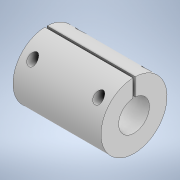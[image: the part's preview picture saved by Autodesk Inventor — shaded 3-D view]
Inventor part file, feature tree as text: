
AUTODESK INVENTOR PART (.ipt)
format: ipt  version: 2021.3 (Build 253353000, 353)  size: 143,360 bytes
history: native  units: mm
features: extrude x3, sketch x3, plane x2
ambient origin geometry x8: Origin, YZ Plane, XZ Plane, XY Plane, X Axis, Y Axis, Z Axis, Center Point
bodies: Solid1 (feature_tree)
feature tree (8):
  extrude  "Extrusion1"  Depth=30.0mm
  plane  "Work Plane1"
  extrude  "Extrusion2"  Depth=0.5mm
  plane  "Work Plane2"
  extrude  "Extrusion3"  Depth=10.0mm TaperAngle=0.0deg
  sketch  "Sketch1"  dims[d0=14.0mm d1=30.0mm]
  sketch  "Sketch3"  dims[d2=20.0mm d3=20.0mm d4=0.0mm d5=0.0mm d10=0.5mm]
  sketch  "Sketch4"  dims[d11=0.5mm d12=20.0mm d13=0.0mm d14=10.0mm d15=15.0mm d16=4.0mm d17=20.0mm d18=0.0mm]
